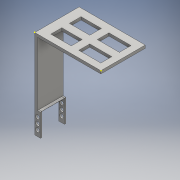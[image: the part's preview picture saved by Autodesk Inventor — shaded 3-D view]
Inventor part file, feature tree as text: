
AUTODESK INVENTOR PART (.ipt)
format: ipt  version: 2016 (Build 200138000, 138)  size: 174,592 bytes
history: native  units: mm
features: sketch x8, extrude x5, hole x1
ambient origin geometry x8: Origin, YZ Plane, XZ Plane, XY Plane, X Axis, Y Axis, Z Axis, Center Point
bodies: Body1 (feature_tree)
feature tree (14):
  extrude  "Extrusion2"  Depth=70.0mm
  extrude  "Extrusion3"  Depth=27.0mm TaperAngle=0.0deg
  extrude  "Extrusion4"  Depth=24.0mm
  extrude  "Extrusion5"  Depth=1.5mm
  extrude  "Extrusion6"  Depth=53.0mm
  sketch  "Sketch11"  dims[d46=32.0mm d47=7.0mm]
  hole  "Hole2"  [1 undecoded]
  sketch  "Sketch13"  dims[d49=10.0mm d50=0.0mm d51=8.0mm d52=8.0mm d53=3.0mm d54=0.0mm d55=4.25mm d56=4.25mm d57=4.25mm d59=6.0mm d60=6.0mm d61=6.0mm d62=4.25mm d63=4.25mm d64=4.25mm d65=6.0mm d66=6.0mm d67=6.0mm d68=4.25mm d69=6.0mm d70=4.0mm d71=2.0mm d72=90.0deg d73=8.0mm d74=0.0mm]
  sketch  "Sketch3"  dims[d26=70.0mm d27=70.0mm]
  sketch  "Sketch4"  dims[d29=6.0mm d31=27.0mm d32=0.0mm]
  sketch  "Sketch5"  dims[d34=20.0mm d35=0.0mm d36=24.0mm]
  sketch  "Sketch9"  dims[d37=24.0mm d38=1.5mm]
  sketch  "Sketch10"  dims[d39=10.0mm d40=0.0mm d45=53.0mm]
  sketch  "Sketch12"  dims[d48=7.0mm]
note: 1 required parameter value undecoded (feature->parameter linkage not recoverable at this tier; creation-order binding heuristic only, values carry confidence <= 0.55)
